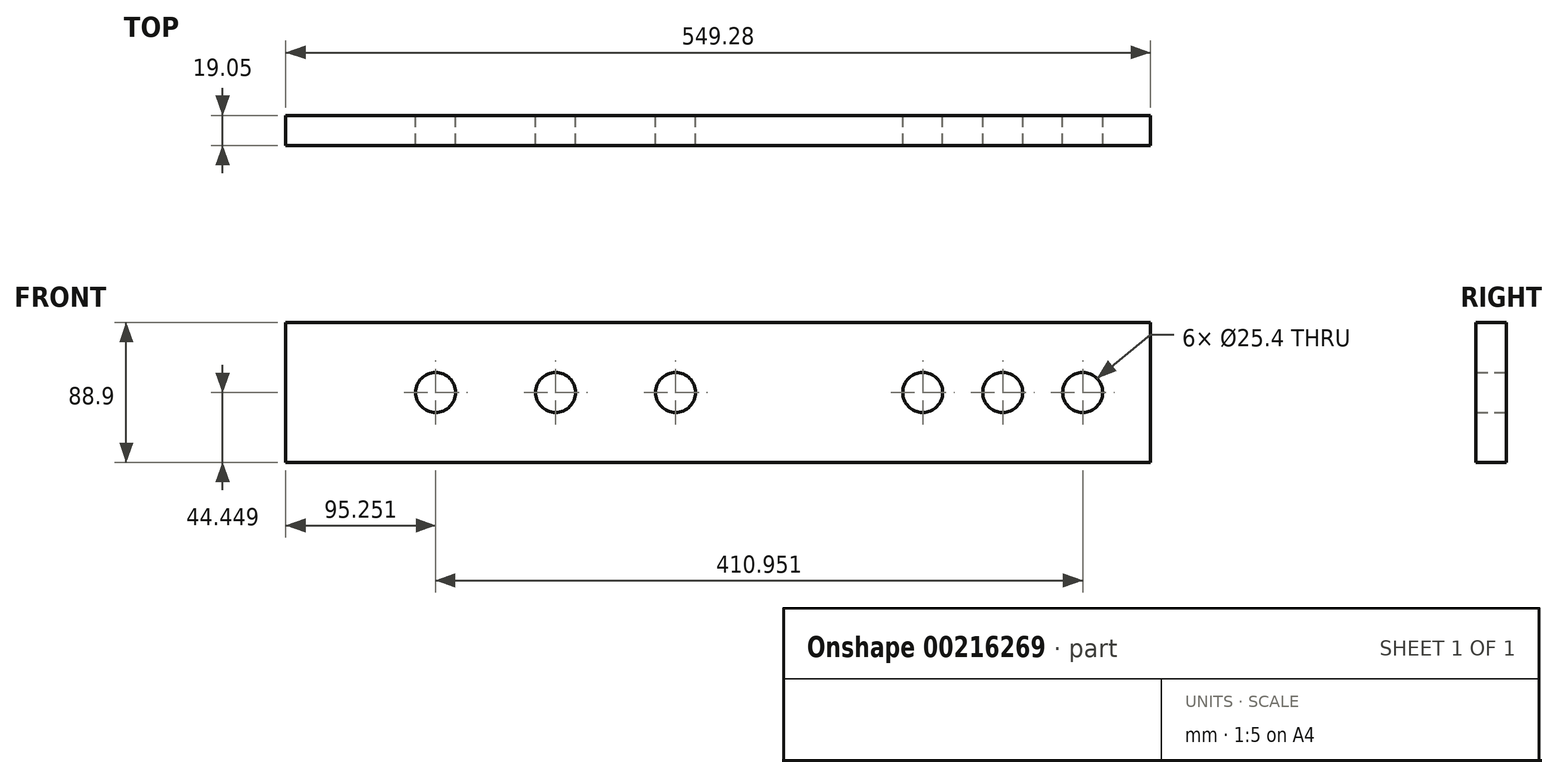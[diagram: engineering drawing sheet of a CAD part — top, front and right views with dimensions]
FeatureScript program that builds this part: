
annotation { "Feature Type Name" : "Feature", "Feature Type Description" : "" }
export const myFeature = defineFeature(function(context is Context, id is Id, definition is map)
    precondition{}
    {
        {
            var Q0;
            Q0=qCreatedBy(makeId("Front.planeOp"),FACE);
            var sketch = newSketch(context, id + "F0", { "sketchPlane" : qUnion([Q0])});
            skLineSegment(sketch, "E0", {"start": v(-1458.24, -455.37) * mm, "end": v(-908.96, -455.37) * mm});
            skLineSegment(sketch, "E1", {"start": v(-908.96, -455.37) * mm, "end": v(-908.96, -366.47) * mm});
            skLineSegment(sketch, "E2", {"start": v(-908.96, -366.47) * mm, "end": v(-1458.24, -366.47) * mm});
            skLineSegment(sketch, "E3", {"start": v(-1458.24, -366.47) * mm, "end": v(-1458.24, -455.37) * mm});
            skCircle(sketch, "E4", {"center": v(-1362.99, -410.92) * mm, "radius": 12.7 * mm});
            skCircle(sketch, "E5", {"center": v(-1286.79, -410.92) * mm, "radius": 12.7 * mm});
            skCircle(sketch, "E6", {"center": v(-1210.59, -410.92) * mm, "radius": 12.7 * mm});
            skCircle(sketch, "E7", {"center": v(-1053.64, -410.92) * mm, "radius": 12.7 * mm});
            skCircle(sketch, "E8", {"center": v(-1002.84, -410.92) * mm, "radius": 12.7 * mm});
            skCircle(sketch, "E9", {"center": v(-952.04, -410.92) * mm, "radius": 12.7 * mm});
            skLineSegment(sketch, "E10", {"start": v(-1458.24, -410.92) * mm, "end": v(-909.39, -410.92) * mm, "construction": true});
            skSolve(sketch);
        }
        {
            var Q0;
            Q0=makeQuery(id+"F0.imprint","IMPRINT",FACE,{"disambiguationData":[TD([[makeQuery(id+"F0.imprint","IMPRINT",EDGE,{"derivedFrom":sQuery(id+"F0.wireOp",EDGE,"E0")}),1.0]])]});
            extrude(context, id + "F1", {"entities" : qUnion([Q0]), "depth" : 19.05 * mm});
        }
    });
